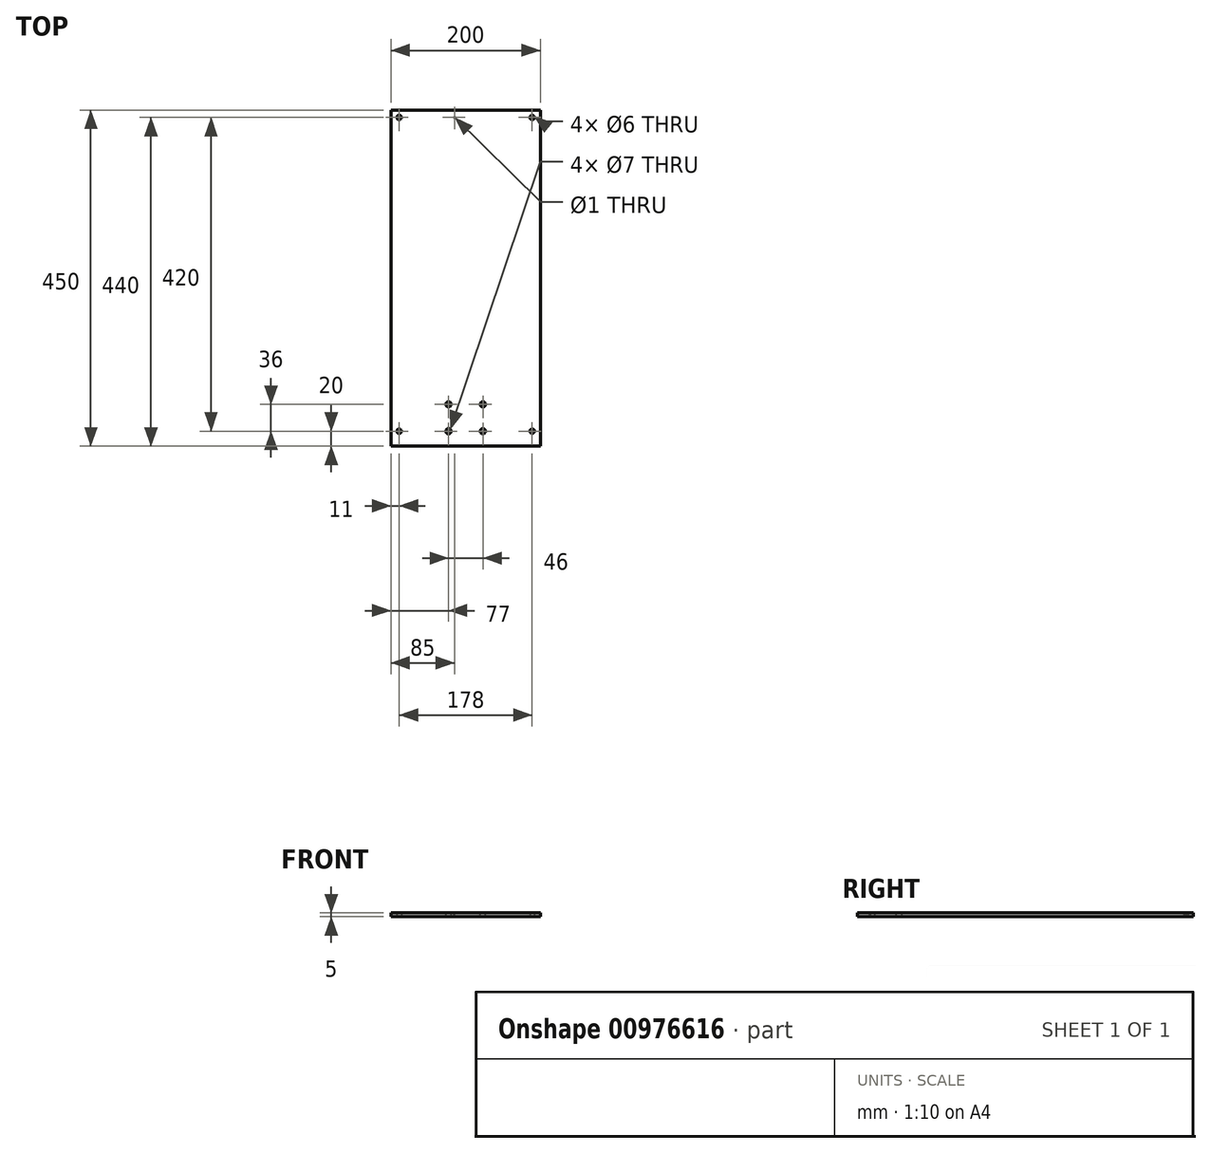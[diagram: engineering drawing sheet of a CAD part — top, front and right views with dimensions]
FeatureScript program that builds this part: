
annotation { "Feature Type Name" : "Feature", "Feature Type Description" : "" }
export const myFeature = defineFeature(function(context is Context, id is Id, definition is map)
    precondition{}
    {
        {
            var Q0;
            Q0=qCreatedBy(makeId("Top.planeOp"),FACE);
            var sketch = newSketch(context, id + "F0", { "sketchPlane" : qUnion([Q0])});
            skLineSegment(sketch, "E0.bottom", {"start": v(100, 225) * mm, "end": v(-100, 225) * mm});
            skLineSegment(sketch, "E0.top", {"start": v(100, -225) * mm, "end": v(-100, -225) * mm});
            skLineSegment(sketch, "E0.left", {"start": v(100, 225) * mm, "end": v(100, -225) * mm});
            skLineSegment(sketch, "E0.right", {"start": v(-100, 225) * mm, "end": v(-100, -225) * mm});
            skPoint(sketch, "E0.middle", {"position": v(0, 0) * mm});
            skPoint(sketch, "E1.middle", {"position": v(0, -225) * mm});
            skCircle(sketch, "E2", {"center": v(-89, -205) * mm, "radius": 3 * mm});
            skCircle(sketch, "E3", {"center": v(89, -205) * mm, "radius": 3 * mm});
            skPoint(sketch, "E4.middle", {"position": v(0, 225) * mm});
            skCircle(sketch, "E5", {"center": v(-89, 215) * mm, "radius": 3 * mm});
            skCircle(sketch, "E6", {"center": v(89, 215) * mm, "radius": 3 * mm});
            skPoint(sketch, "E4.top.end.orphan", {"position": v(-89, 235) * mm});
            skPoint(sketch, "E7.orphan", {"position": v(89, 235) * mm});
            skPoint(sketch, "E1.top.end.orphan", {"position": v(-89, -245) * mm});
            skPoint(sketch, "E8.orphan", {"position": v(89, -245) * mm});
            skSolve(sketch);
        }
        {
            var Q0;
            Q0=makeQuery(id+"F0.imprint","IMPRINT",FACE,{"disambiguationData":[TD([[makeQuery(id+"F0.imprint","IMPRINT",EDGE,{"derivedFrom":sQuery(id+"F0.wireOp",EDGE,"E0.bottom")}),1.0]])]});
            extrude(context, id + "F1", {"entities" : qUnion([Q0]), "depth" : 5 * mm, "offsetDistance" : 25 * mm});
        }
        {
            var Q0;
            Q0=makeQuery(id+"F1.opExtrude","CAP_FACE",FACE,{"disambiguationData":[OSD([sQuery(id+"F0.wireOp",EDGE,"E0.bottom"),sQuery(id+"F0.wireOp",EDGE,"E0.top"),sQuery(id+"F0.wireOp",EDGE,"E0.left"),sQuery(id+"F0.wireOp",EDGE,"E0.right")])],"isStart":false});
            var sketch = newSketch(context, id + "F2", { "sketchPlane" : qUnion([Q0])});
            skLineSegment(sketch, "E9", {"start": v(0, -225) * mm, "end": v(0, -205) * mm});
            skLineSegment(sketch, "E10", {"start": v(0, -205) * mm, "end": v(23, -205) * mm});
            skLineSegment(sketch, "E11", {"start": v(23, -205) * mm, "end": v(23, -169) * mm});
            skLineSegment(sketch, "E12", {"start": v(23, -169) * mm, "end": v(-23, -169) * mm});
            skLineSegment(sketch, "E13", {"start": v(-23, -169) * mm, "end": v(-23, -205) * mm});
            skCircle(sketch, "E14", {"center": v(23, -169) * mm, "radius": 3.5 * mm});
            skCircle(sketch, "E15", {"center": v(-23, -169) * mm, "radius": 3.5 * mm});
            skCircle(sketch, "E16", {"center": v(-23, -205) * mm, "radius": 3.5 * mm});
            skCircle(sketch, "E17", {"center": v(23, -205) * mm, "radius": 3.5 * mm});
            skSolve(sketch);
        }
        {
            var Q0;
            {var subQ0=sQuery(id+"F2.wireOp",EDGE,"E13");var subQ1=sQuery(id+"F2.wireOp",EDGE,"E12");var subQ2=makeQuery(id+"F2.imprint","INTERSECT",VERTEX,{"derivedFrom":[subQ1,subQ0]});Q0=makeQuery(id+"F2.imprint","IMPRINT",FACE,{"disambiguationData":[TD([[makeQuery(id+"F2.imprint","IMPRINT",EDGE,{"disambiguationData":[TD([[subQ2,1.0]])],"derivedFrom":subQ1}),-1.0]])]});}
            var Q1;
            {var subQ0=sQuery(id+"F2.wireOp",EDGE,"E13");var subQ1=sQuery(id+"F2.wireOp",EDGE,"E12");var subQ2=makeQuery(id+"F2.imprint","INTERSECT",VERTEX,{"derivedFrom":[subQ1,subQ0]});Q1=makeQuery(id+"F2.imprint","IMPRINT",FACE,{"disambiguationData":[TD([[makeQuery(id+"F2.imprint","IMPRINT",EDGE,{"disambiguationData":[TD([[subQ2,1.0]])],"derivedFrom":subQ1}),1.0]])]});}
            var Q2;
            {var subQ0=sQuery(id+"F2.wireOp",EDGE,"E12");var subQ1=sQuery(id+"F2.wireOp",EDGE,"E11");var subQ2=makeQuery(id+"F2.imprint","INTERSECT",VERTEX,{"derivedFrom":[subQ1,subQ0]});Q2=makeQuery(id+"F2.imprint","IMPRINT",FACE,{"disambiguationData":[TD([[makeQuery(id+"F2.imprint","IMPRINT",EDGE,{"disambiguationData":[TD([[subQ2,1.0]])],"derivedFrom":subQ1}),-1.0]])]});}
            var Q3;
            {var subQ0=sQuery(id+"F2.wireOp",EDGE,"E12");var subQ1=sQuery(id+"F2.wireOp",EDGE,"E11");var subQ2=makeQuery(id+"F2.imprint","INTERSECT",VERTEX,{"derivedFrom":[subQ1,subQ0]});Q3=makeQuery(id+"F2.imprint","IMPRINT",FACE,{"disambiguationData":[TD([[makeQuery(id+"F2.imprint","IMPRINT",EDGE,{"disambiguationData":[TD([[subQ2,1.0]])],"derivedFrom":subQ1}),1.0]])]});}
            var Q4;
            {var subQ0=sQuery(id+"F2.wireOp",EDGE,"E11");var subQ1=sQuery(id+"F2.wireOp",EDGE,"E10");var subQ2=makeQuery(id+"F2.imprint","INTERSECT",VERTEX,{"derivedFrom":[subQ1,subQ0]});Q4=makeQuery(id+"F2.imprint","IMPRINT",FACE,{"disambiguationData":[TD([[makeQuery(id+"F2.imprint","IMPRINT",EDGE,{"disambiguationData":[TD([[subQ2,1.0]])],"derivedFrom":subQ1}),1.0]])]});}
            var Q5;
            Q5=makeQuery(id+"F2.imprint","IMPRINT",FACE,{"disambiguationData":[TD([[makeQuery(id+"F2.imprint","IMPRINT",EDGE,{"derivedFrom":sQuery(id+"F2.wireOp",EDGE,"E16")}),1.0]])]});
            var Q6;
            {var subQ0=sQuery(id+"F2.wireOp",EDGE,"E11");var subQ1=sQuery(id+"F2.wireOp",EDGE,"E10");var subQ2=makeQuery(id+"F2.imprint","INTERSECT",VERTEX,{"derivedFrom":[subQ1,subQ0]});Q6=makeQuery(id+"F2.imprint","IMPRINT",FACE,{"disambiguationData":[TD([[makeQuery(id+"F2.imprint","IMPRINT",EDGE,{"disambiguationData":[TD([[subQ2,1.0]])],"derivedFrom":subQ1}),-1.0]])]});}
            extrude(context, id + "F3", {"entities" : qUnion([Q0, Q1, Q2, Q3, Q4, Q5, Q6]), "operationType" : NewBodyOperationType.REMOVE, "endBound" : BoundingType.THROUGH_ALL, "oppositeDirection" : true, "depth" : 25 * mm, "offsetDistance" : 25 * mm});
        }
        {
            var Q0;
            Q0=makeQuery(id+"F1.opExtrude","CAP_FACE",FACE,{"disambiguationData":[OSD([sQuery(id+"F0.wireOp",EDGE,"E0.bottom"),sQuery(id+"F0.wireOp",EDGE,"E0.top"),sQuery(id+"F0.wireOp",EDGE,"E0.left"),sQuery(id+"F0.wireOp",EDGE,"E0.right"),sQuery(id+"F0.wireOp",EDGE,"E2"),sQuery(id+"F0.wireOp",EDGE,"E3"),sQuery(id+"F0.wireOp",EDGE,"E5"),sQuery(id+"F0.wireOp",EDGE,"E6")])],"isStart":false});
            var sketch = newSketch(context, id + "F4", { "sketchPlane" : qUnion([Q0])});
            skLineSegment(sketch, "E18", {"start": v(0, 225) * mm, "end": v(-15, 225) * mm});
            skLineSegment(sketch, "E19", {"start": v(-15, 225) * mm, "end": v(-15, 215) * mm});
            skCircle(sketch, "E20", {"center": v(-15, 215) * mm, "radius": 0.5 * mm});
            skSolve(sketch);
        }
        {
            var Q0;
            Q0 = qSketchRegion(id + "F4", true);
            extrude(context, id + "F5", {"entities" : qUnion([Q0]), "operationType" : NewBodyOperationType.REMOVE, "oppositeDirection" : true, "depth" : 25 * mm, "offsetDistance" : 25 * mm});
        }
    });
